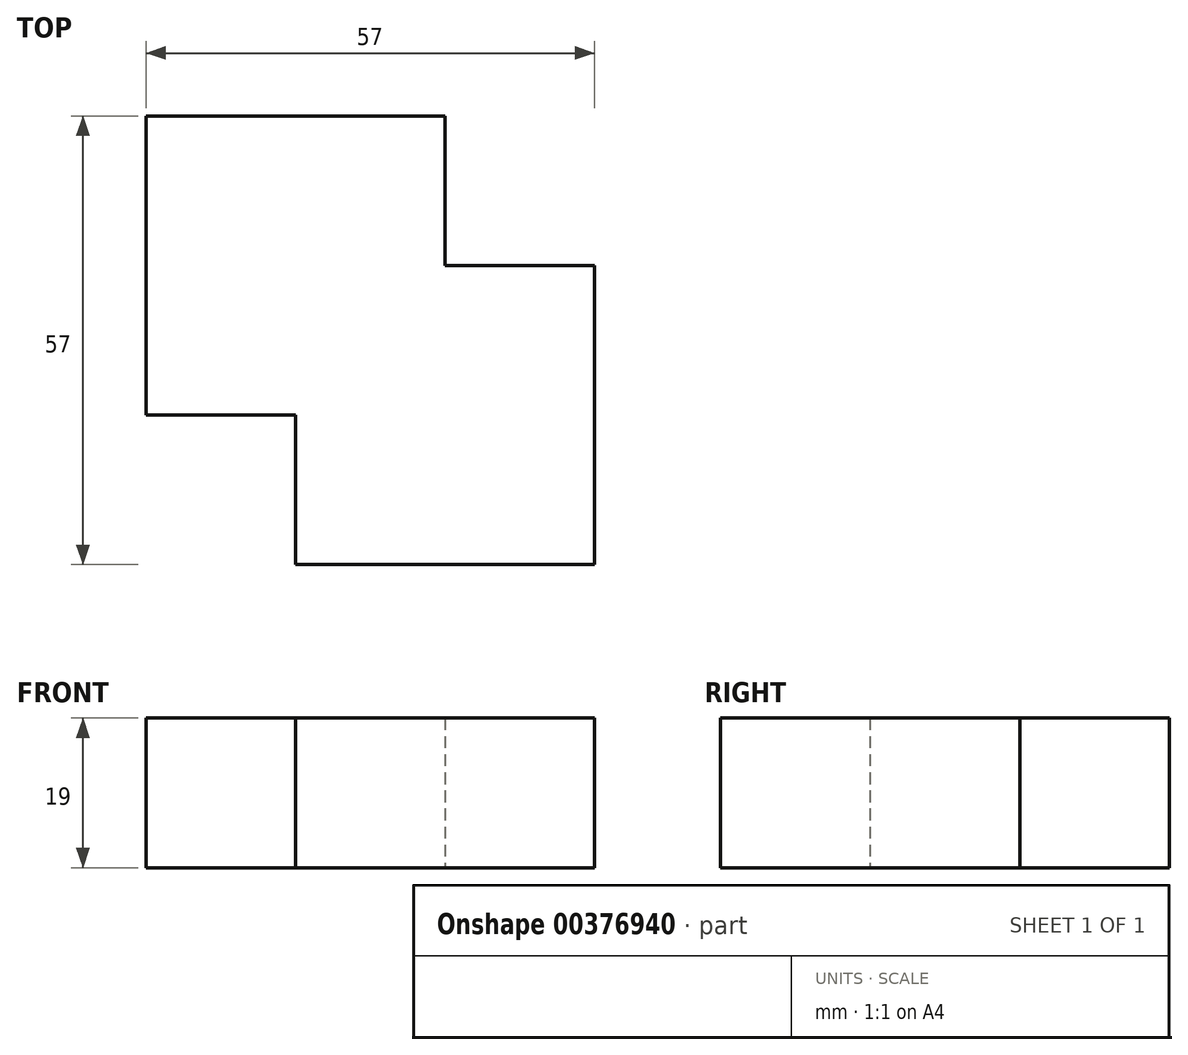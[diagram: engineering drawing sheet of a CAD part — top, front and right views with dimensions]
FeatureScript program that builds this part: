
annotation { "Feature Type Name" : "Feature", "Feature Type Description" : "" }
export const myFeature = defineFeature(function(context is Context, id is Id, definition is map)
    precondition{}
    {
        {
            var Q0;
            Q0=qCreatedBy(makeId("Top.planeOp"),FACE);
            var sketch = newSketch(context, id + "F0", { "sketchPlane" : qUnion([Q0])});
            skPoint(sketch, "E0.middle", {"position": v(0, 0) * mm});
            skLineSegment(sketch, "E1", {"start": v(-28.5, 28.5) * mm, "end": v(-28.5, -9.5) * mm});
            skLineSegment(sketch, "E2", {"start": v(-28.5, -9.5) * mm, "end": v(-9.5, -9.5) * mm});
            skLineSegment(sketch, "E3", {"start": v(-9.5, -9.5) * mm, "end": v(-9.5, -28.5) * mm});
            skLineSegment(sketch, "E4", {"start": v(-9.5, -28.5) * mm, "end": v(28.5, -28.5) * mm});
            skLineSegment(sketch, "E5", {"start": v(-28.5, 28.5) * mm, "end": v(9.5, 28.5) * mm});
            skLineSegment(sketch, "E6", {"start": v(9.5, 28.5) * mm, "end": v(9.5, 9.5) * mm});
            skLineSegment(sketch, "E7", {"start": v(9.5, 9.5) * mm, "end": v(28.5, 9.5) * mm});
            skLineSegment(sketch, "E8", {"start": v(28.5, 9.5) * mm, "end": v(28.5, -28.5) * mm});
            skSolve(sketch);
        }
        {
            var Q0;
            Q0 = qSketchRegion(id + "F0", true);
            extrude(context, id + "F1", {"entities" : qUnion([Q0]), "endBound" : BoundingType.SYMMETRIC, "depth" : 19 * mm});
        }
    });
